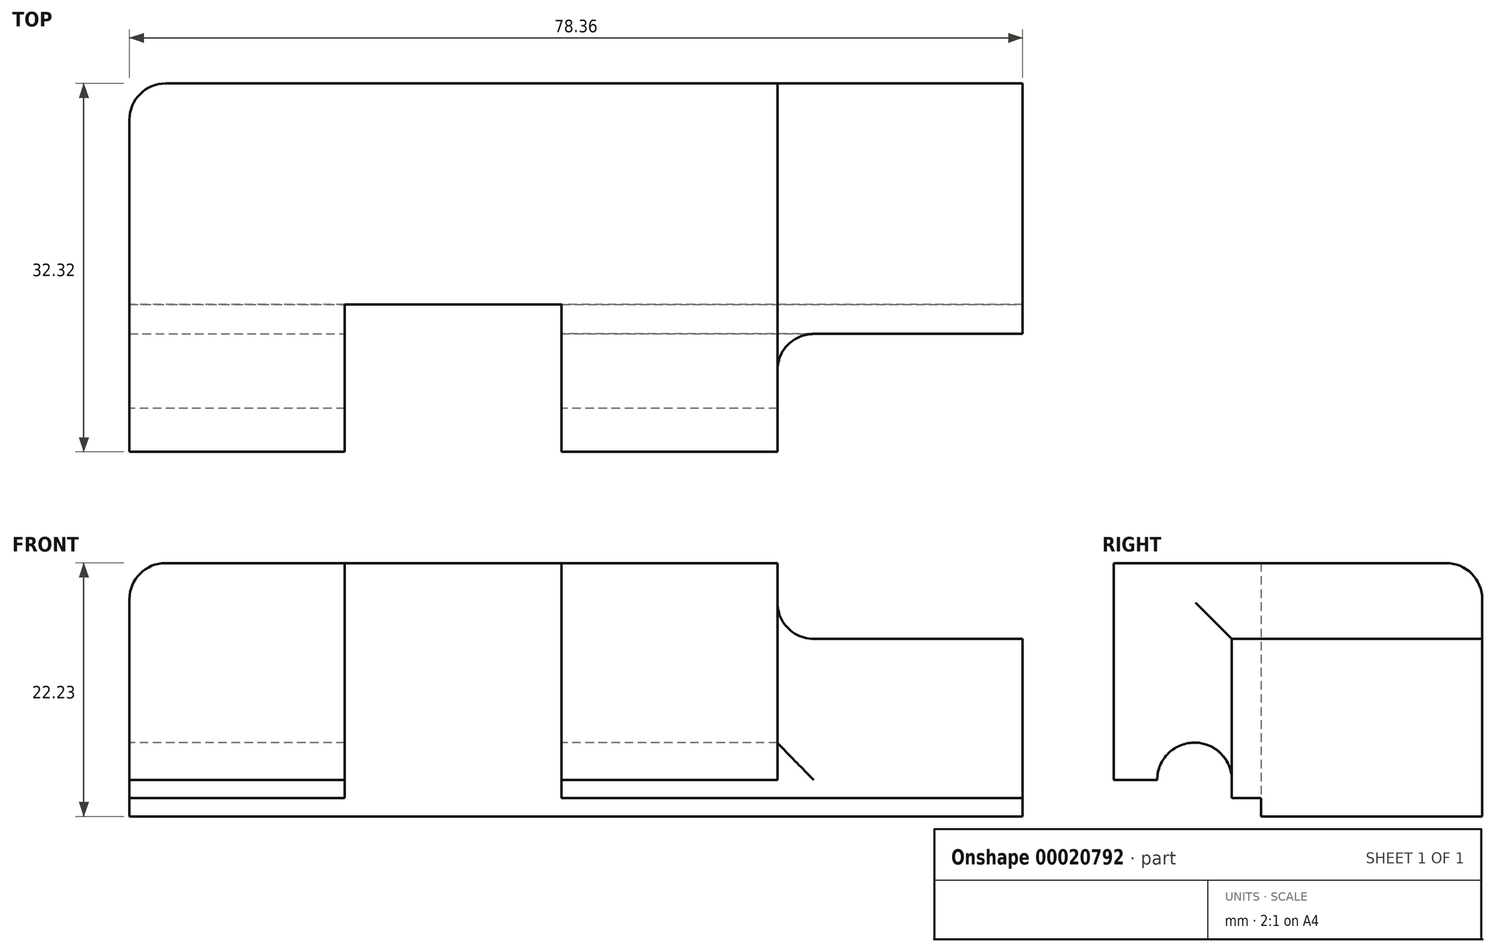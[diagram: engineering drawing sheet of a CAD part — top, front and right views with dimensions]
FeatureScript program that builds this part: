
annotation { "Feature Type Name" : "Feature", "Feature Type Description" : "" }
export const myFeature = defineFeature(function(context is Context, id is Id, definition is map)
    precondition{}
    {
        {
            var Q0;
            Q0=qCreatedBy(makeId("Top.planeOp"),FACE);
            var sketch = newSketch(context, id + "F0", { "sketchPlane" : qUnion([Q0])});
            skLineSegment(sketch, "E0", {"start": v(0, 0) * mm, "end": v(0, -32.32) * mm});
            skLineSegment(sketch, "E1", {"start": v(0, -32.32) * mm, "end": v(18.9, -32.32) * mm});
            skLineSegment(sketch, "E2", {"start": v(18.9, -32.32) * mm, "end": v(18.9, -19.4) * mm});
            skLineSegment(sketch, "E3", {"start": v(18.9, -19.4) * mm, "end": v(37.9, -19.4) * mm});
            skLineSegment(sketch, "E4", {"start": v(37.9, -19.4) * mm, "end": v(37.9, -32.32) * mm});
            skLineSegment(sketch, "E5", {"start": v(37.9, -32.32) * mm, "end": v(56.85, -32.32) * mm});
            skLineSegment(sketch, "E6", {"start": v(56.85, -32.32) * mm, "end": v(56.85, -21.97) * mm});
            skLineSegment(sketch, "E7", {"start": v(56.85, -21.97) * mm, "end": v(78.36, -21.97) * mm});
            skLineSegment(sketch, "E8", {"start": v(78.36, -21.97) * mm, "end": v(78.36, 0) * mm});
            skLineSegment(sketch, "E9", {"start": v(78.36, 0) * mm, "end": v(0, 0) * mm});
            skSolve(sketch);
        }
        {
            var Q0;
            Q0 = qSketchRegion(id + "F0", true);
            extrude(context, id + "F1", {"entities" : qUnion([Q0]), "depth" : 22.22 * mm});
        }
        {
            var Q0;
            Q0=makeQuery(id+"F1.opExtrude","CAP_EDGE",EDGE,{"disambiguationData":[OSD([sQuery(id+"F0.wireOp",EDGE,"E0")])],"isStart":false});
            var Q1;
            Q1=makeQuery(id+"F1.opExtrude","SWEPT_EDGE",EDGE,{"disambiguationData":[OSD([sQuery(id+"F0.wireOp",EDGE,"E0"),sQuery(id+"F0.wireOp",EDGE,"E9")])]});
            var Q2;
            Q2=makeQuery(id+"F1.opExtrude","CAP_EDGE",EDGE,{"disambiguationData":[OSD([sQuery(id+"F0.wireOp",EDGE,"E9")])],"isStart":false});
            fillet(context, id + "F2", {"entities" : qUnion([Q0, Q1, Q2]), "radius" : 3.17 * mm, "tangentPropagation" : true, "allowEdgeOverflow" : false});
        }
        {
            var Q0;
            Q0=makeQuery(id+"F1.opExtrude","CAP_FACE",FACE,{"disambiguationData":[OSD([sQuery(id+"F0.wireOp",EDGE,"E0"),sQuery(id+"F0.wireOp",EDGE,"E1"),sQuery(id+"F0.wireOp",EDGE,"E2"),sQuery(id+"F0.wireOp",EDGE,"E3"),sQuery(id+"F0.wireOp",EDGE,"E4"),sQuery(id+"F0.wireOp",EDGE,"E5"),sQuery(id+"F0.wireOp",EDGE,"E6"),sQuery(id+"F0.wireOp",EDGE,"E7"),sQuery(id+"F0.wireOp",EDGE,"E8"),sQuery(id+"F0.wireOp",EDGE,"E9")])],"isStart":true});
            var sketch = newSketch(context, id + "F3", { "sketchPlane" : qUnion([Q0])});
            skLineSegment(sketch, "E10", {"start": v(78.36, 19.4) * mm, "end": v(0, 19.4) * mm});
            skLineSegment(sketch, "E11", {"start": v(0, 19.4) * mm, "end": v(0, 32.32) * mm});
            skLineSegment(sketch, "E12", {"start": v(0, 32.32) * mm, "end": v(18.9, 32.32) * mm});
            skLineSegment(sketch, "E13", {"start": v(18.9, 32.32) * mm, "end": v(18.9, 19.4) * mm});
            skLineSegment(sketch, "E14", {"start": v(18.9, 19.4) * mm, "end": v(37.9, 19.4) * mm});
            skLineSegment(sketch, "E15", {"start": v(37.9, 19.4) * mm, "end": v(37.9, 32.32) * mm});
            skLineSegment(sketch, "E16", {"start": v(37.9, 32.32) * mm, "end": v(56.85, 32.32) * mm});
            skLineSegment(sketch, "E17", {"start": v(56.85, 32.32) * mm, "end": v(56.85, 21.97) * mm});
            skLineSegment(sketch, "E18", {"start": v(56.85, 21.97) * mm, "end": v(78.36, 21.97) * mm});
            skLineSegment(sketch, "E19", {"start": v(78.36, 21.97) * mm, "end": v(78.36, 19.4) * mm});
            skSolve(sketch);
        }
        {
            var Q0;
            Q0 = qSketchRegion(id + "F3", true);
            extrude(context, id + "F4", {"entities" : qUnion([Q0]), "operationType" : NewBodyOperationType.REMOVE, "oppositeDirection" : true, "depth" : 1.6 * mm});
        }
        {
            var Q0;
            Q0=makeQuery(id+"F1.opExtrude","SWEPT_FACE",FACE,{"disambiguationData":[OSD([sQuery(id+"F0.wireOp",EDGE,"E7")])]});
            var sketch = newSketch(context, id + "F5", { "sketchPlane" : qUnion([Q0])});
            skLineSegment(sketch, "E20.bottom", {"start": v(56.85, 22.23) * mm, "end": v(78.36, 22.23) * mm});
            skLineSegment(sketch, "E20.top", {"start": v(56.85, 15.57) * mm, "end": v(78.36, 15.57) * mm});
            skLineSegment(sketch, "E20.left", {"start": v(56.85, 22.23) * mm, "end": v(56.85, 15.57) * mm});
            skLineSegment(sketch, "E20.right", {"start": v(78.36, 22.23) * mm, "end": v(78.36, 15.57) * mm});
            skSolve(sketch);
        }
        {
            var Q0;
            Q0=makeQuery(id+"F5.imprint","IMPRINT",FACE,{"disambiguationData":[TD([[makeQuery(id+"F5.imprint","IMPRINT",EDGE,{"derivedFrom":sQuery(id+"F5.wireOp",EDGE,"E20.bottom")}),-1.0]])]});
            extrude(context, id + "F6", {"entities" : qUnion([Q0]), "operationType" : NewBodyOperationType.REMOVE, "endBound" : BoundingType.UP_TO_NEXT, "oppositeDirection" : true, "depth" : 25.4 * mm});
        }
        {
            var Q0;
            {var subQ0=sQuery(id+"F0.wireOp",EDGE,"E6");Q0=makeQuery(id+"F6.boolean.opBoolean","MERGE",EDGE,{"derivedFrom":[makeQuery(id+"F1.opExtrude","CAP_EDGE",EDGE,{"disambiguationData":[OSD([subQ0])],"isStart":false}),makeQuery(id+"F6.opExtrude","SWEPT_EDGE",EDGE,{"disambiguationData":[OSD([subQ0,sQuery(id+"F0.wireOp",EDGE,"E7"),sQuery(id+"F5.wireOp",EDGE,"E20.bottom"),sQuery(id+"F5.wireOp",EDGE,"E20.left")])]})]});}
            var Q1;
            Q1=makeQuery(id+"F6.boolean.opBoolean","COPY",EDGE,{"derivedFrom":makeQuery(id+"F6.opExtrude","SWEPT_EDGE",EDGE,{"disambiguationData":[OSD([sQuery(id+"F0.wireOp",EDGE,"E6"),sQuery(id+"F0.wireOp",EDGE,"E7"),sQuery(id+"F5.wireOp",EDGE,"E20.top"),sQuery(id+"F5.wireOp",EDGE,"E20.left")])]})});
            var Q2;
            Q2=makeQuery(id+"F1.opExtrude","SWEPT_EDGE",EDGE,{"disambiguationData":[OSD([sQuery(id+"F0.wireOp",EDGE,"E6"),sQuery(id+"F0.wireOp",EDGE,"E7")])]});
            fillet(context, id + "F7", {"entities" : qUnion([Q0, Q1, Q2]), "radius" : 3.17 * mm, "allowEdgeOverflow" : false});
        }
        {
            var Q0;
            Q0=makeQuery(id+"F4.boolean.opBoolean","COPY",FACE,{"derivedFrom":makeQuery(id+"F4.opExtrude","CAP_FACE",FACE,{"disambiguationData":[OSD([sQuery(id+"F3.wireOp",EDGE,"E10"),sQuery(id+"F3.wireOp",EDGE,"E11"),sQuery(id+"F3.wireOp",EDGE,"E12"),sQuery(id+"F3.wireOp",EDGE,"E13")])],"isStart":false})});
            var sketch = newSketch(context, id + "F8", { "sketchPlane" : qUnion([Q0])});
            skLineSegment(sketch, "E21.bottom", {"start": v(0, 32.32) * mm, "end": v(56.85, 32.32) * mm});
            skLineSegment(sketch, "E21.top", {"start": v(0, 27.24) * mm, "end": v(56.85, 27.24) * mm});
            skLineSegment(sketch, "E21.left", {"start": v(0, 32.32) * mm, "end": v(0, 27.24) * mm});
            skLineSegment(sketch, "E21.right", {"start": v(56.85, 32.32) * mm, "end": v(56.85, 27.24) * mm});
            skSolve(sketch);
        }
        {
            var Q0;
            Q0 = qSketchRegion(id + "F8", true);
            extrude(context, id + "F9", {"entities" : qUnion([Q0]), "operationType" : NewBodyOperationType.REMOVE, "oppositeDirection" : true, "depth" : 1.6 * mm});
        }
        {
            var Q0;
            Q0=makeQuery(id+"F1.opExtrude","SWEPT_FACE",FACE,{"disambiguationData":[OSD([sQuery(id+"F0.wireOp",EDGE,"E0")])]});
            var sketch = newSketch(context, id + "F10", { "sketchPlane" : qUnion([Q0])});
            skLineSegment(sketch, "E22", {"start": v(28.51, 7.7) * mm, "end": v(28.51, -3.48) * mm, "construction": true});
            skLineSegment(sketch, "E23", {"start": v(21.97, 8.18) * mm, "end": v(21.97, -6.6) * mm, "construction": true});
            skLineSegment(sketch, "E24", {"start": v(28.51, 3.2) * mm, "end": v(21.97, 3.2) * mm, "construction": true});
            skArc(sketch, "E25", {"start": v(28.51, 3.2) * mm, "mid": v(25.24, 6.47) * mm, "end": v(21.97, 3.2) * mm});
            skLineSegment(sketch, "E26", {"start": v(21.97, 3.2) * mm, "end": v(21.97, -2.33) * mm});
            skLineSegment(sketch, "E27", {"start": v(21.97, -2.33) * mm, "end": v(28.51, -2.33) * mm});
            skLineSegment(sketch, "E28", {"start": v(28.51, -2.33) * mm, "end": v(28.51, 3.2) * mm});
            skSolve(sketch);
        }
        {
            var Q0;
            Q0 = qSketchRegion(id + "F10", true);
            extrude(context, id + "F11", {"entities" : qUnion([Q0]), "operationType" : NewBodyOperationType.REMOVE, "endBound" : BoundingType.THROUGH_ALL, "oppositeDirection" : true, "depth" : 25.4 * mm});
        }
    });
